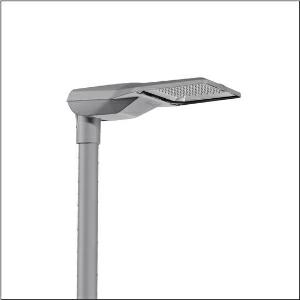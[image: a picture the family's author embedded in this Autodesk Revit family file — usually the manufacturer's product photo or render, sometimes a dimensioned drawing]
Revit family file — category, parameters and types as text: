
# Revit family: streetlight_sl_21_midi___st1_0ab_5xe7m33a08mb_9819
name_source: partatom
category: Lighting Fixtures
units: mm (PartAtom-declared; Revit-internal decimal feet)

## family parameters
Cut with Voids When Loaded = No
Host = Face
Light Source = No
Part Type = Normal
Room Calculation Point = No
Round Connector Dimension = Use Diameter
Shared = No

## types (1)
- --- (1 x LED, 16080 lm, 136 W, 3000K)
    Apparent Load = 136 VA
    CIE Flux Codes = 38 73 97 100 100
    Color Rendering = 70
    Color Temperature = 3000K
    Default Elevation = 1800 mm
    Description = Streetlight SL 21 midi, mast luminaire, primary light control with lens, of PMMA, primary optical cover: cover, of toughened safety glass, transparent, light distribution: ST1.0aB, light emission: direct distribution, primary light characteristic: asymmetric, installation type: post-top, side-entry, LED, 3G 1.5mm², High Power LED, rated luminous flux: 16.080lm, luminous efficacy: 118lm/W, light colour: 730, colour temperature: 3000K, control: flexible luminous flux parameterisation, time-dependent luminous flux control, constant luminous flux control, overheat protection, mains connection: 220..240V, AC, 50/60Hz, connection cable pre-assembled, cable length: 12,5m, wiring characteristics: H07RN-F, start of lifetime: 136W, end of service life: 142W, reduction: 61W, luminaire housing, of diecast aluminium, powder-coated, Siteco® metallic grey (DB 702S), corrosivity category C5 mid according to DIN EN ISO 12944, please order mast flange separately, inclination adjustable: 0°, 5°, 10°, 15°, sealing non-destructively replaceable, multi-level sealing system, length: 644mm, width: 335mm, height: 110mm, mast flange for spigot size: 42mm (side-entry): 5XC10008XM4, 60/48mm (side-entry/post-top): 5XC10108XM2, 76/60mm (side-entry/post-top): 5XC10108XM1, protection rating (complete): IP66, insulation class (complete): insulation class II (safety insulation), certification: CE, ENEC, ENEC+, VDE, impact resistance: IK09, permissible operating ambient temperature for outdoor applications: -40..+50°C, standard-compliant lighting for roads and squares, packaging unit: 1 piece

Light Distribution: ST1.0aB
    Height = 111 mm
    Lamp = 1 x LED
    Lamp Light Flux = 16080 lm
    Lamp Power = 136 W
    Lamp count = 1
    Length = 644 mm
    Luminous efficacy = 118 lm/W
    Manufacturer = Siteco
    ModVariant = No
    Model = 5XE7M33A08MB
    Number of Poles = 1
    OnlyDefault = Yes
    Power Factor = 1
    Product Name = Streetlight SL 21 midi | ST1.0aB
    Product group = mast luminaire | pylon top
    ProductGroupID = 6100
    Protection Class = Protection class II
    Protection Degree = IP 66
    RLX_Detail_Level = 1
    RLX_Emergency_Light_Flux = 0 lm
    RLX_Emergency_Type = 0
    RLX_Emergency_Type_DB = No
    RlxData = <blob elided: 90421 chars, md5=dcd85278>
    Socket = socket
    Standby Power = 0 W
    System Light Flux = 16081 lm
    System Power = 136 W
    Type Comments = factory setting: luminous flux: 100 % | Output Level: 100 % | 695 mA
    Type Image = l_1004298.jpg
    URL = http://relux.com
    VarID = @adj_134251
    Voltage = 0 V
    Weight = 0.00 kg
    Width = 336 mm

## geometry (parser evidence)
native form markers: Blend x4, Sweep x13
no freeform markers — native parametric forms only
